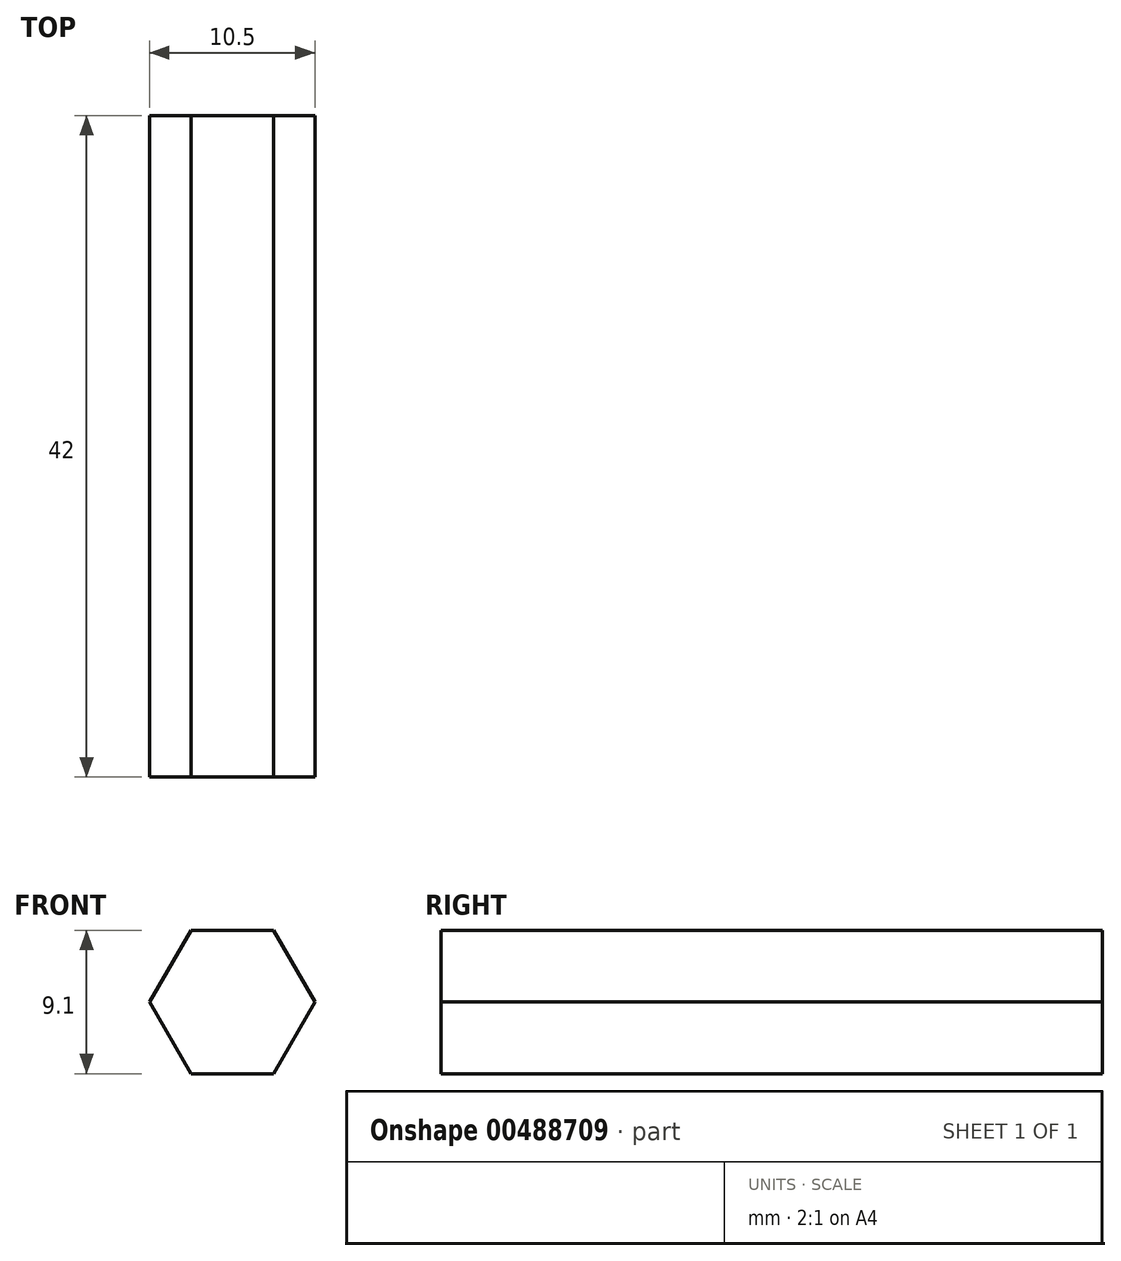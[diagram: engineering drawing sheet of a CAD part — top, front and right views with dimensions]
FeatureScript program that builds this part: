
annotation { "Feature Type Name" : "Feature", "Feature Type Description" : "" }
export const myFeature = defineFeature(function(context is Context, id is Id, definition is map)
    precondition{}
    {
        {
            var Q0;
            Q0=qCreatedBy(makeId("Front.planeOp"),FACE);
            var sketch = newSketch(context, id + "F0", { "sketchPlane" : qUnion([Q0])});
            skCircle(sketch, "E0.cCircle", {"center": v(0, 0) * mm, "radius": 5.25 * mm, "construction": true});
            skLineSegment(sketch, "E0.0", {"start": v(-5.25, 0) * mm, "end": v(-2.62, 4.55) * mm});
            skLineSegment(sketch, "E0.1", {"start": v(-2.63, 4.55) * mm, "end": v(2.62, 4.55) * mm});
            skLineSegment(sketch, "E0.2", {"start": v(2.62, 4.55) * mm, "end": v(5.25, 0) * mm});
            skLineSegment(sketch, "E0.3", {"start": v(5.25, 0) * mm, "end": v(2.63, -4.55) * mm});
            skLineSegment(sketch, "E0.4", {"start": v(2.63, -4.55) * mm, "end": v(-2.62, -4.55) * mm});
            skLineSegment(sketch, "E0.5", {"start": v(-2.62, -4.55) * mm, "end": v(-5.25, 0) * mm});
            skSolve(sketch);
        }
        {
            var Q0;
            Q0=makeQuery(id+"F0.imprint","IMPRINT",FACE,{"disambiguationData":[TD([[makeQuery(id+"F0.imprint","IMPRINT",EDGE,{"derivedFrom":sQuery(id+"F0.wireOp",EDGE,"E0.0")}),-1.0]])]});
            extrude(context, id + "F1", {"entities" : qUnion([Q0]), "endBound" : BoundingType.SYMMETRIC, "depth" : 42 * mm});
        }
    });
